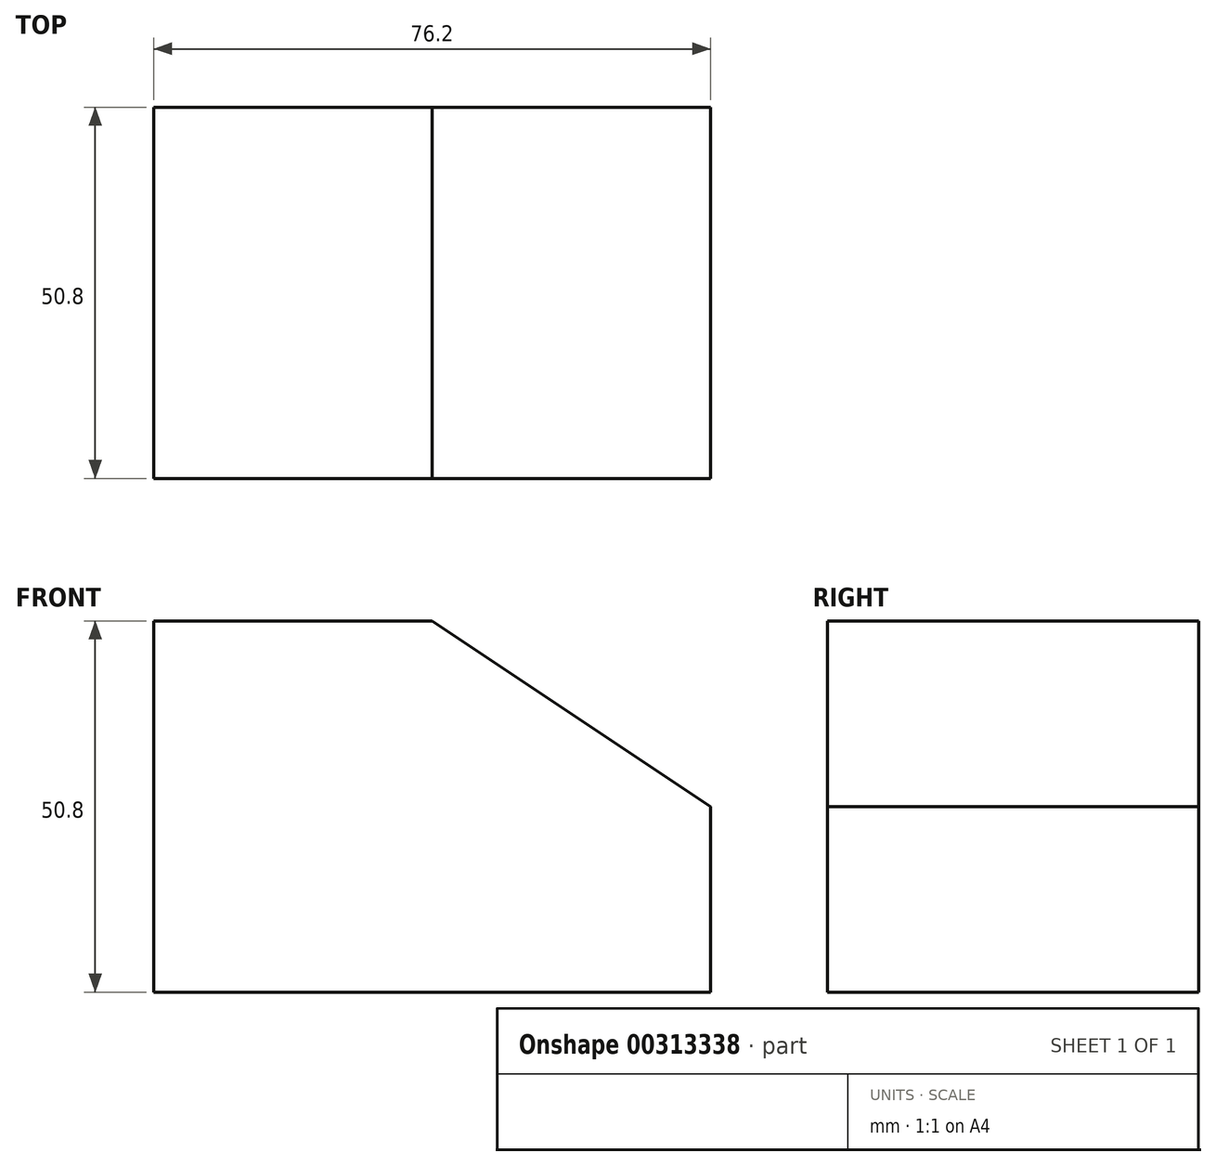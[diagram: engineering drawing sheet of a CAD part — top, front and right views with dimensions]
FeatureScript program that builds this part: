
annotation { "Feature Type Name" : "Feature", "Feature Type Description" : "" }
export const myFeature = defineFeature(function(context is Context, id is Id, definition is map)
    precondition{}
    {
        {
            var Q0;
            Q0=qCreatedBy(makeId("Front.planeOp"),FACE);
            var sketch = newSketch(context, id + "F0", { "sketchPlane" : qUnion([Q0])});
            skLineSegment(sketch, "E0", {"start": v(-40.89, -70.41) * mm, "end": v(35.31, -70.41) * mm});
            skLineSegment(sketch, "E1", {"start": v(-40.89, -70.41) * mm, "end": v(-40.89, -19.61) * mm});
            skLineSegment(sketch, "E2", {"start": v(-40.89, -19.61) * mm, "end": v(-2.79, -19.61) * mm});
            skLineSegment(sketch, "E3", {"start": v(35.31, -70.41) * mm, "end": v(35.31, -45.01) * mm});
            skLineSegment(sketch, "E4", {"start": v(-2.79, -19.61) * mm, "end": v(35.31, -45.01) * mm});
            skSolve(sketch);
        }
        {
            var Q0;
            Q0=makeQuery(id+"F0.imprint","IMPRINT",FACE,{"disambiguationData":[TD([[makeQuery(id+"F0.imprint","IMPRINT",EDGE,{"derivedFrom":sQuery(id+"F0.wireOp",EDGE,"E0")}),1.0]])]});
            extrude(context, id + "F1", {"entities" : qUnion([Q0]), "depth" : 50.8 * mm});
        }
    });
